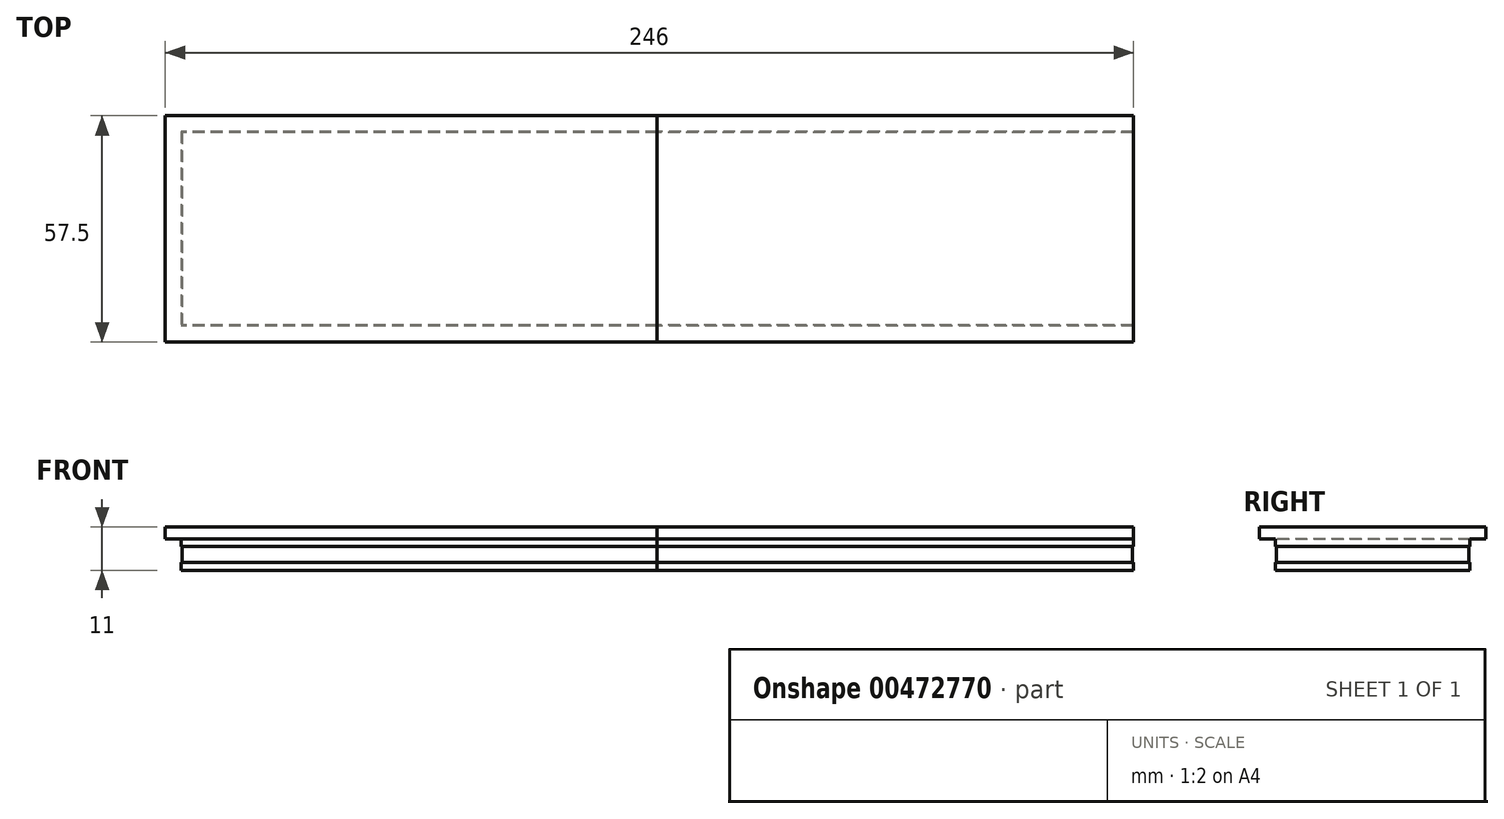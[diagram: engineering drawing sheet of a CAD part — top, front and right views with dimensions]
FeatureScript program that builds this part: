
annotation { "Feature Type Name" : "Feature", "Feature Type Description" : "" }
export const myFeature = defineFeature(function(context is Context, id is Id, definition is map)
    precondition{}
    {
        {
            var Q0;
            Q0=qCreatedBy(makeId("Top.planeOp"),FACE);
            var sketch = newSketch(context, id + "F0", { "sketchPlane" : qUnion([Q0])});
            skLineSegment(sketch, "E0.bottom", {"start": v(121, 24.75) * mm, "end": v(-121, 24.75) * mm});
            skLineSegment(sketch, "E0.top", {"start": v(121, -24.75) * mm, "end": v(-121, -24.75) * mm});
            skLineSegment(sketch, "E0.left", {"start": v(121, 24.75) * mm, "end": v(121, -24.75) * mm});
            skLineSegment(sketch, "E0.right", {"start": v(-121, 24.75) * mm, "end": v(-121, -24.75) * mm});
            skPoint(sketch, "E0.middle", {"position": v(0, 0) * mm});
            skSolve(sketch);
        }
        {
            var Q0;
            Q0=makeQuery(id+"F0.imprint","IMPRINT",FACE,{"disambiguationData":[TD([[makeQuery(id+"F0.imprint","IMPRINT",EDGE,{"derivedFrom":sQuery(id+"F0.wireOp",EDGE,"E0.bottom")}),1.0]])]});
            extrude(context, id + "F1", {"entities" : qUnion([Q0]), "depth" : 2 * mm, "offsetDistance" : 25 * mm});
        }
        {
            var Q0;
            Q0=makeQuery(id+"F1.opExtrude","CAP_FACE",FACE,{"disambiguationData":[OSD([sQuery(id+"F0.wireOp",EDGE,"E0.bottom"),sQuery(id+"F0.wireOp",EDGE,"E0.top"),sQuery(id+"F0.wireOp",EDGE,"E0.left"),sQuery(id+"F0.wireOp",EDGE,"E0.right")])],"isStart":false});
            var sketch = newSketch(context, id + "F2", { "sketchPlane" : qUnion([Q0])});
            skLineSegment(sketch, "E1.bottom", {"start": v(120.75, 24.5) * mm, "end": v(-120.75, 24.5) * mm});
            skLineSegment(sketch, "E1.top", {"start": v(120.75, -24.5) * mm, "end": v(-120.75, -24.5) * mm});
            skLineSegment(sketch, "E1.left", {"start": v(120.75, 24.5) * mm, "end": v(120.75, -24.5) * mm});
            skLineSegment(sketch, "E1.right", {"start": v(-120.75, 24.5) * mm, "end": v(-120.75, -24.5) * mm});
            skPoint(sketch, "E1.middle", {"position": v(0, 0) * mm});
            skSolve(sketch);
        }
        {
            var Q0;
            Q0=makeQuery(id+"F2.imprint","IMPRINT",FACE,{"disambiguationData":[TD([[makeQuery(id+"F2.imprint","IMPRINT",EDGE,{"derivedFrom":sQuery(id+"F2.wireOp",EDGE,"E1.bottom")}),1.0]])]});
            extrude(context, id + "F3", {"entities" : qUnion([Q0]), "operationType" : NewBodyOperationType.ADD, "depth" : 4 * mm, "offsetDistance" : 25 * mm});
        }
        {
            var Q0;
            Q0=makeQuery(id+"F3.opExtrude","CAP_FACE",FACE,{"disambiguationData":[OSD([sQuery(id+"F2.wireOp",EDGE,"E1.bottom"),sQuery(id+"F2.wireOp",EDGE,"E1.top"),sQuery(id+"F2.wireOp",EDGE,"E1.left"),sQuery(id+"F2.wireOp",EDGE,"E1.right")])],"isStart":false});
            var sketch = newSketch(context, id + "F4", { "sketchPlane" : qUnion([Q0])});
            skLineSegment(sketch, "E2.bottom", {"start": v(121, 24.75) * mm, "end": v(-121, 24.75) * mm});
            skLineSegment(sketch, "E2.top", {"start": v(121, -24.75) * mm, "end": v(-121, -24.75) * mm});
            skLineSegment(sketch, "E2.left", {"start": v(121, 24.75) * mm, "end": v(121, -24.75) * mm});
            skLineSegment(sketch, "E2.right", {"start": v(-121, 24.75) * mm, "end": v(-121, -24.75) * mm});
            skPoint(sketch, "E2.middle", {"position": v(0, 0) * mm});
            skSolve(sketch);
        }
        {
            var Q0;
            Q0=qSketchRegion(id+"F4",true);
            extrude(context, id + "F5", {"entities" : qUnion([Q0]), "operationType" : NewBodyOperationType.ADD, "depth" : 2 * mm, "offsetDistance" : 25 * mm});
        }
        {
            var Q0;
            Q0=makeQuery(id+"F5.opExtrude","CAP_FACE",FACE,{"disambiguationData":[OSD([sQuery(id+"F4.wireOp",EDGE,"E2.bottom"),sQuery(id+"F4.wireOp",EDGE,"E2.top"),sQuery(id+"F4.wireOp",EDGE,"E2.left"),sQuery(id+"F4.wireOp",EDGE,"E2.right")])],"isStart":false});
            var sketch = newSketch(context, id + "F6", { "sketchPlane" : qUnion([Q0])});
            skLineSegment(sketch, "E3.bottom", {"start": v(-121, 24.75) * mm, "end": v(121, 24.75) * mm});
            skLineSegment(sketch, "E3.top", {"start": v(-121, 28.75) * mm, "end": v(121, 28.75) * mm});
            skLineSegment(sketch, "E3.left", {"start": v(-121, 24.75) * mm, "end": v(-121, 28.75) * mm});
            skLineSegment(sketch, "E3.right", {"start": v(121, 24.75) * mm, "end": v(121, 28.75) * mm});
            skLineSegment(sketch, "E4.bottom", {"start": v(-121, -24.75) * mm, "end": v(121, -24.75) * mm});
            skLineSegment(sketch, "E4.top", {"start": v(-121, -28.75) * mm, "end": v(121, -28.75) * mm});
            skLineSegment(sketch, "E4.left", {"start": v(-121, -24.75) * mm, "end": v(-121, -28.75) * mm});
            skLineSegment(sketch, "E4.right", {"start": v(121, -24.75) * mm, "end": v(121, -28.75) * mm});
            skLineSegment(sketch, "E5.bottom", {"start": v(-121, -28.75) * mm, "end": v(-125, -28.75) * mm});
            skLineSegment(sketch, "E5.top", {"start": v(-121, 28.75) * mm, "end": v(-125, 28.75) * mm});
            skLineSegment(sketch, "E5.left", {"start": v(-121, -28.75) * mm, "end": v(-121, 28.75) * mm});
            skLineSegment(sketch, "E5.right", {"start": v(-125, -28.75) * mm, "end": v(-125, 28.75) * mm});
            skSolve(sketch);
        }
        {
            var Q0;
            Q0=qSketchRegion(id+"F6",true);
            var Q1;
            {var subQ0=sQuery(id+"F6.wireOp",EDGE,"E3.bottom");Q1=makeQuery(id+"F6.imprint","IMPRINT",FACE,{"disambiguationData":[TD([[makeQuery(id+"F6.imprint","IMPRINT",EDGE,{"derivedFrom":subQ0}),1.0]])]});}
            extrude(context, id + "F7", {"entities" : qUnion([Q0, Q1]), "operationType" : NewBodyOperationType.ADD, "depth" : 3 * mm, "offsetDistance" : 25 * mm});
        }
        {
            var Q0;
            Q0=makeQuery(id+"F7.opExtrude","CAP_FACE",FACE,{"disambiguationData":[OSD([sQuery(id+"F4.wireOp",EDGE,"E2.left"),sQuery(id+"F6.wireOp",EDGE,"E3.top"),sQuery(id+"F6.wireOp",EDGE,"E3.right"),sQuery(id+"F6.wireOp",EDGE,"E4.top"),sQuery(id+"F6.wireOp",EDGE,"E4.right"),sQuery(id+"F6.wireOp",EDGE,"E5.bottom"),sQuery(id+"F6.wireOp",EDGE,"E5.top"),sQuery(id+"F6.wireOp",EDGE,"E5.right")])],"isStart":false});
            var sketch = newSketch(context, id + "F8", { "sketchPlane" : qUnion([Q0])});
            skLineSegment(sketch, "E6.bottom", {"start": v(0, -28.75) * mm, "end": v(0, -28.75) * mm});
            skLineSegment(sketch, "E6.top", {"start": v(0, 28.75) * mm, "end": v(0, 28.75) * mm});
            skLineSegment(sketch, "E6.left", {"start": v(0, -28.75) * mm, "end": v(0, 28.75) * mm});
            skLineSegment(sketch, "E6.right", {"start": v(0, -28.75) * mm, "end": v(0, 28.75) * mm});
            skPoint(sketch, "E6.middle", {"position": v(0, 0) * mm});
            skSolve(sketch);
        }
        {
            var Q0;
            Q0 = qSketchRegion(id + "F8", true);
            extrude(context, id + "F9", {"entities" : qUnion([Q0]), "operationType" : NewBodyOperationType.REMOVE, "oppositeDirection" : true, "depth" : 25 * mm, "offsetDistance" : 25 * mm});
        }
    });
